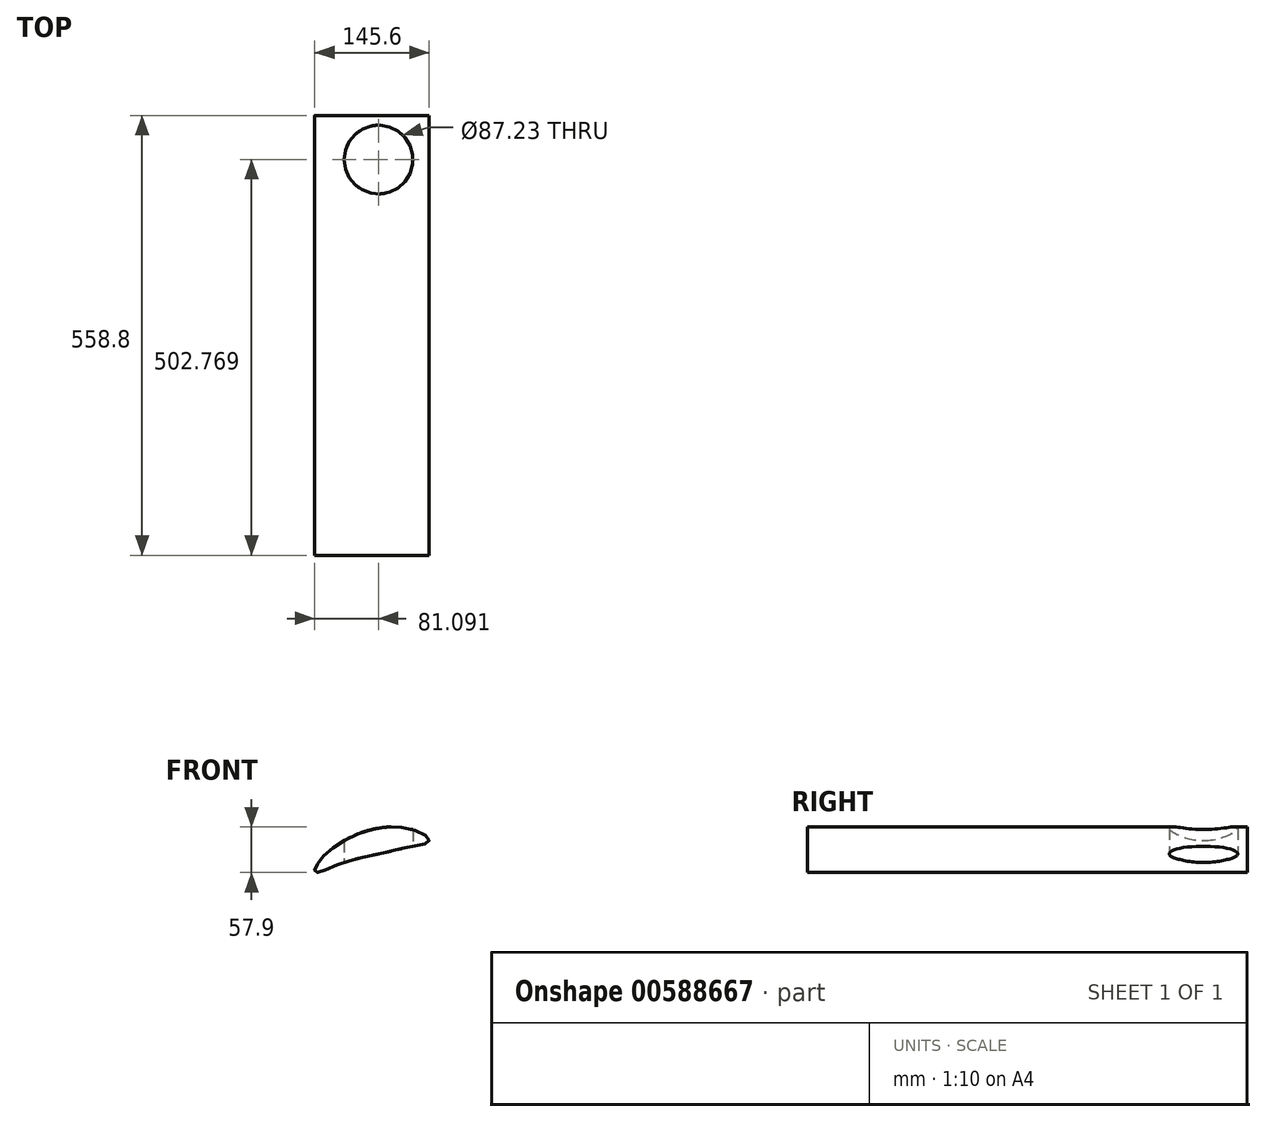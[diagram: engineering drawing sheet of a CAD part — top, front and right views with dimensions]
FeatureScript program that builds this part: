
annotation { "Feature Type Name" : "Feature", "Feature Type Description" : "" }
export const myFeature = defineFeature(function(context is Context, id is Id, definition is map)
    precondition{}
    {
        {
            var Q0;
            Q0=qCreatedBy(makeId("Front.planeOp"),FACE);
            var sketch = newSketch(context, id + "F0", { "sketchPlane" : qUnion([Q0])});
            skFitSpline(sketch, "E0", {"points": [v(-93.82, 0) * mm, v(-52.3, 33.7) * mm, v(22.2, 44.9) * mm, v(48.29, 29.2) * mm, v(24.43, 21.68) * mm, v(-9.98, 13.85) * mm, v(-65.09, 0) * mm, v(-96.33, -10.54) * mm, v(-93.82, 0) * mm]});
            skPoint(sketch, "E1.1.internal.orphan", {"position": v(-9.98, 4.9) * mm});
            skSolve(sketch);
        }
        {
            var Q0;
            Q0=makeQuery(id+"F0.imprint","IMPRINT",FACE,{"disambiguationData":[TD([[makeQuery(id+"F0.imprint","IMPRINT",EDGE,{"derivedFrom":sQuery(id+"F0.wireOp",EDGE,"E0")}),-1.0]])]});
            extrude(context, id + "F1", {"entities" : qUnion([Q0]), "depth" : 558.8 * mm, "offsetDistance" : 25.4 * mm});
        }
        {
            var Q0;
            Q0=qCreatedBy(makeId("Top.planeOp"),FACE);
            var sketch = newSketch(context, id + "F2", { "sketchPlane" : qUnion([Q0])});
            skCircle(sketch, "E2", {"center": v(-16.14, -56.03) * mm, "radius": 43.61 * mm});
            skSolve(sketch);
        }
        {
            var Q0;
            Q0 = qSketchRegion(id + "F2", true);
            extrude(context, id + "F3", {"entities" : qUnion([Q0]), "operationType" : NewBodyOperationType.REMOVE, "depth" : 76.2 * mm, "offsetDistance" : 25.4 * mm});
        }
    });
